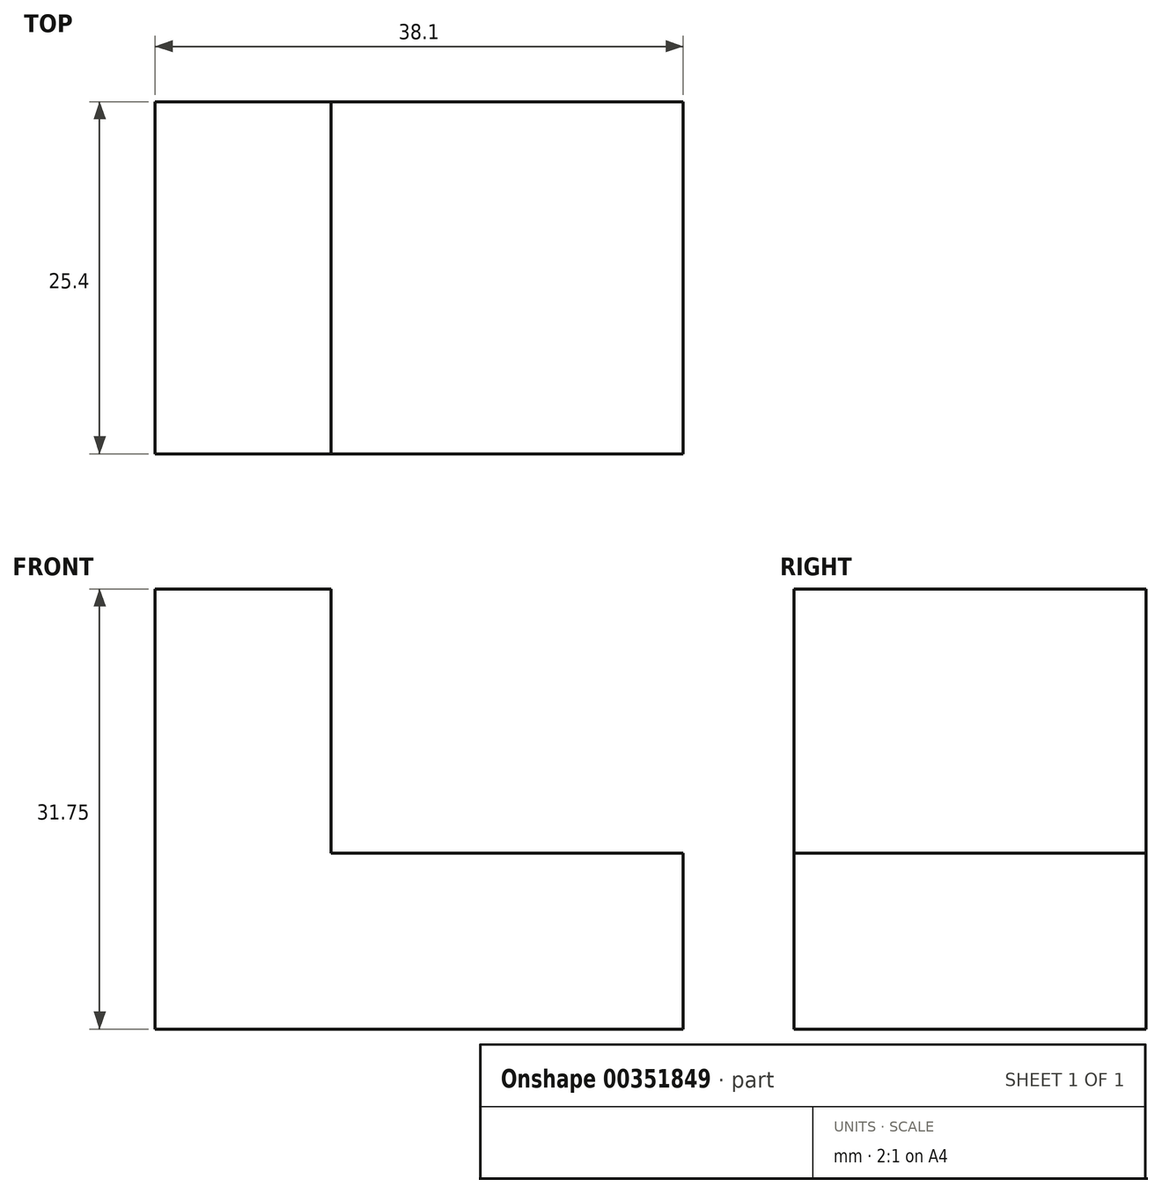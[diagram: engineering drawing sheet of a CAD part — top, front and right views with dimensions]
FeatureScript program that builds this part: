
annotation { "Feature Type Name" : "Feature", "Feature Type Description" : "" }
export const myFeature = defineFeature(function(context is Context, id is Id, definition is map)
    precondition{}
    {
        {
            var Q0;
            Q0=qCreatedBy(makeId("Front.planeOp"),FACE);
            var sketch = newSketch(context, id + "F0", { "sketchPlane" : qUnion([Q0])});
            skLineSegment(sketch, "E0.bottom", {"start": v(0, 0) * mm, "end": v(12.7, 0) * mm});
            skLineSegment(sketch, "E0.top", {"start": v(0, 31.75) * mm, "end": v(12.7, 31.75) * mm});
            skLineSegment(sketch, "E0.left", {"start": v(0, 0) * mm, "end": v(0, 31.75) * mm});
            skLineSegment(sketch, "E0.right", {"start": v(12.7, 0) * mm, "end": v(12.7, 31.75) * mm});
            skLineSegment(sketch, "E1.bottom", {"start": v(0, 0) * mm, "end": v(38.1, 0) * mm});
            skLineSegment(sketch, "E1.top", {"start": v(0, 12.7) * mm, "end": v(38.1, 12.7) * mm});
            skLineSegment(sketch, "E1.left", {"start": v(0, 0) * mm, "end": v(0, 12.7) * mm});
            skLineSegment(sketch, "E1.right", {"start": v(38.1, 0) * mm, "end": v(38.1, 12.7) * mm});
            skSolve(sketch);
        }
        {
            var Q0;
            Q0 = qSketchRegion(id + "F0", true);
            extrude(context, id + "F1", {"entities" : qUnion([Q0]), "depth" : 25.4 * mm});
        }
    });
